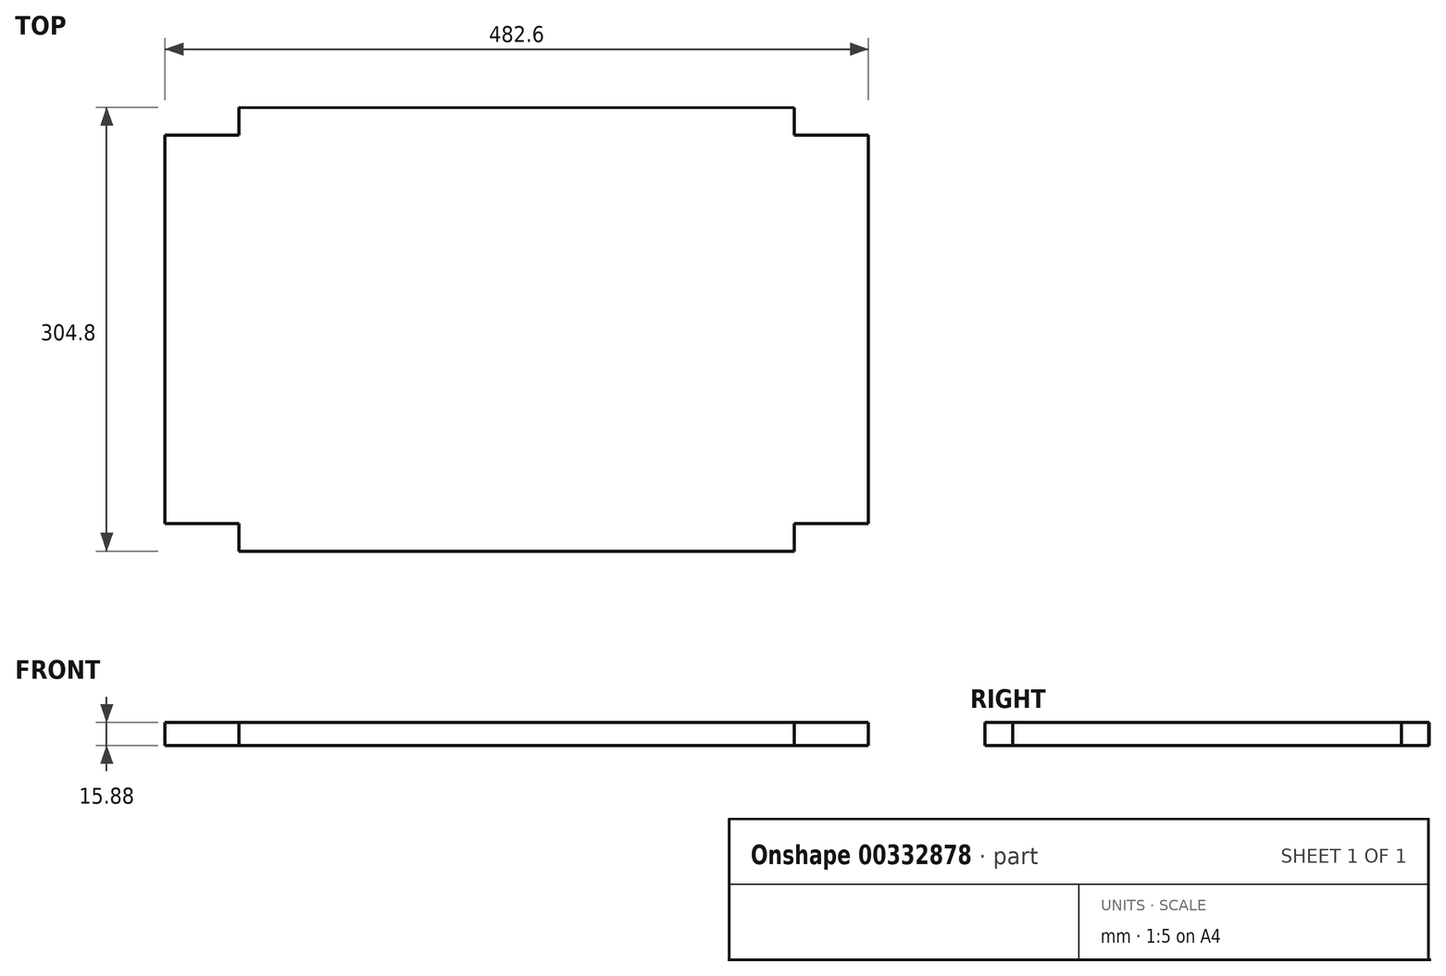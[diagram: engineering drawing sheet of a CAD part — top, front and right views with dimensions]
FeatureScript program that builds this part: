
annotation { "Feature Type Name" : "Feature", "Feature Type Description" : "" }
export const myFeature = defineFeature(function(context is Context, id is Id, definition is map)
    precondition{}
    {
        {
            var Q0;
            Q0=qCreatedBy(makeId("Top.planeOp"),FACE);
            var sketch = newSketch(context, id + "F0", { "sketchPlane" : qUnion([Q0])});
            skLineSegment(sketch, "E0.bottom", {"start": v(-190.5, -83.33) * mm, "end": v(190.5, -83.33) * mm});
            skLineSegment(sketch, "E0.left", {"start": v(-241.3, -64.28) * mm, "end": v(-241.3, 202.42) * mm});
            skLineSegment(sketch, "E0.right", {"start": v(241.3, -64.28) * mm, "end": v(241.3, 202.42) * mm});
            skPoint(sketch, "E0.middle", {"position": v(0, 0) * mm});
            skLineSegment(sketch, "E1.top", {"start": v(-241.3, 202.42) * mm, "end": v(-190.5, 202.42) * mm});
            skLineSegment(sketch, "E1.right", {"start": v(-190.5, 221.47) * mm, "end": v(-190.5, 202.42) * mm});
            skLineSegment(sketch, "E2.bottom", {"start": v(-190.5, -64.28) * mm, "end": v(-241.3, -64.28) * mm});
            skLineSegment(sketch, "E2.left", {"start": v(-190.5, -64.28) * mm, "end": v(-190.5, -83.33) * mm});
            skLineSegment(sketch, "E3.top", {"start": v(241.3, 202.42) * mm, "end": v(190.5, 202.42) * mm});
            skLineSegment(sketch, "E3.right", {"start": v(190.5, 221.2) * mm, "end": v(190.5, 202.42) * mm});
            skLineSegment(sketch, "E4.bottom", {"start": v(190.5, -64.28) * mm, "end": v(241.3, -64.28) * mm});
            skLineSegment(sketch, "E4.left", {"start": v(190.5, -64.28) * mm, "end": v(190.5, -83.33) * mm});
            skPoint(sketch, "E5.trimOffspring.end.orphan", {"position": v(241.3, 83.33) * mm});
            skPoint(sketch, "E6.orphan", {"position": v(241.3, -83.33) * mm});
            skPoint(sketch, "E7.orphan", {"position": v(-241.3, -83.33) * mm});
            skPoint(sketch, "E8.orphan", {"position": v(-241.3, 83.33) * mm});
            skLineSegment(sketch, "E9", {"start": v(190.5, 221.2) * mm, "end": v(-190.5, 221.47) * mm});
            skSolve(sketch);
        }
        {
            var Q0;
            Q0=qSketchRegion(id+"F0",true);
            extrude(context, id + "F1", {"entities" : qUnion([Q0]), "depth" : 15.88 * mm});
        }
    });
